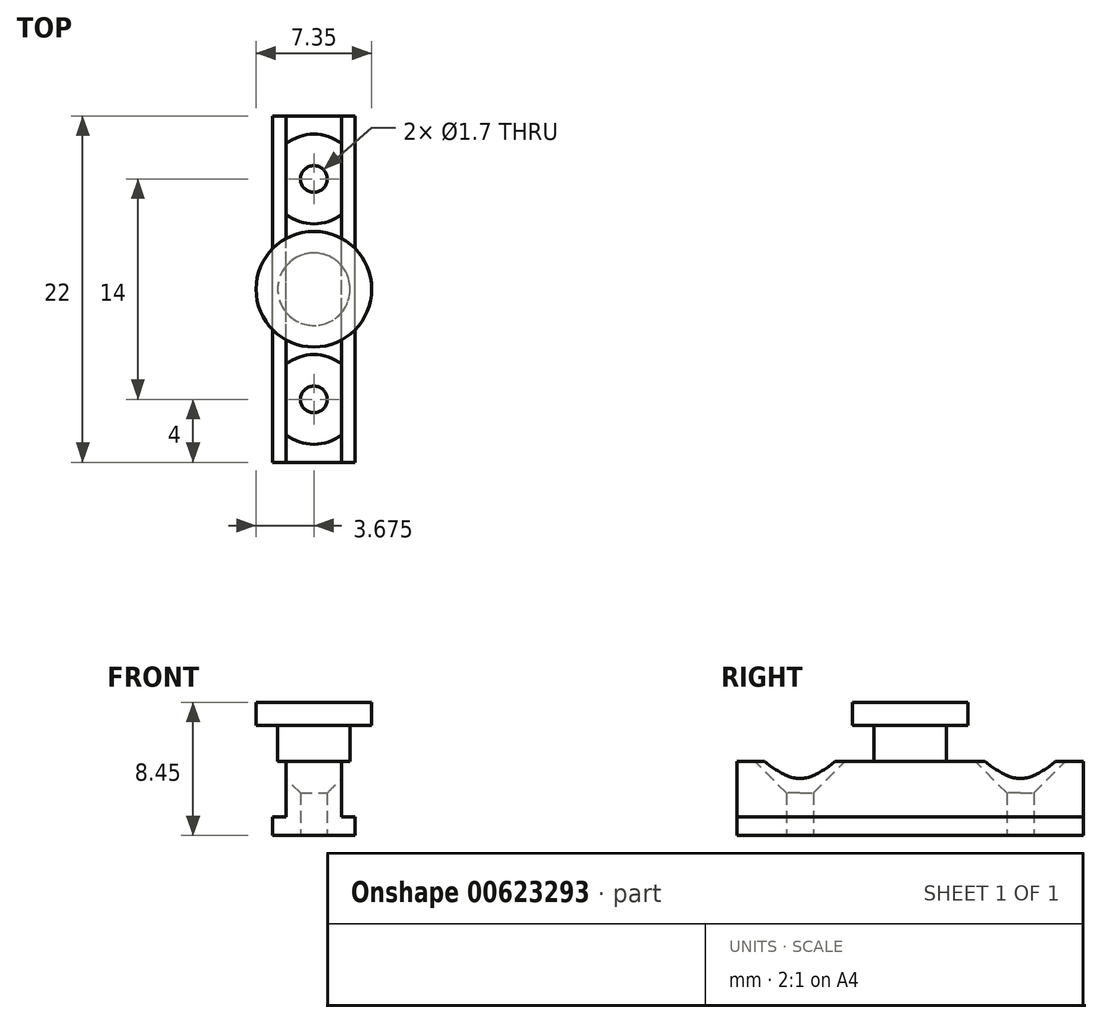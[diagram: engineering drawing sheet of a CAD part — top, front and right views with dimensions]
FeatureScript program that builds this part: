
annotation { "Feature Type Name" : "Feature", "Feature Type Description" : "" }
export const myFeature = defineFeature(function(context is Context, id is Id, definition is map)
    precondition{}
    {
        {
            var Q0;
            Q0=qCreatedBy(makeId("Front.planeOp"),FACE);
            var sketch = newSketch(context, id + "F0", { "sketchPlane" : qUnion([Q0])});
            skLineSegment(sketch, "E0.bottom", {"start": v(-39.65, 22.37) * mm, "end": v(-36.12, 22.37) * mm});
            skLineSegment(sketch, "E0.top", {"start": v(-39.65, 17.67) * mm, "end": v(-36.12, 17.67) * mm});
            skLineSegment(sketch, "E0.left", {"start": v(-39.65, 22.37) * mm, "end": v(-39.65, 18.84) * mm});
            skLineSegment(sketch, "E0.right", {"start": v(-36.12, 22.37) * mm, "end": v(-36.12, 18.84) * mm});
            skLineSegment(sketch, "E1.bottom", {"start": v(-36.12, 17.67) * mm, "end": v(-35.26, 17.67) * mm});
            skLineSegment(sketch, "E1.top", {"start": v(-36.12, 18.84) * mm, "end": v(-35.26, 18.84) * mm});
            skLineSegment(sketch, "E1.right", {"start": v(-35.26, 17.67) * mm, "end": v(-35.26, 18.84) * mm});
            skLineSegment(sketch, "E2.bottom", {"start": v(-39.65, 17.67) * mm, "end": v(-40.5, 17.67) * mm});
            skLineSegment(sketch, "E2.top", {"start": v(-39.65, 18.84) * mm, "end": v(-40.5, 18.84) * mm});
            skLineSegment(sketch, "E2.right", {"start": v(-40.5, 17.67) * mm, "end": v(-40.5, 18.84) * mm});
            skSolve(sketch);
        }
        {
            var Q0;
            Q0 = qSketchRegion(id + "F0", true);
            extrude(context, id + "F1", {"entities" : qUnion([Q0]), "depth" : 22 * mm, "offsetDistance" : 25 * mm});
        }
        {
            var Q0;
            Q0=makeQuery(id+"F1.opExtrude","SWEPT_FACE",FACE,{"disambiguationData":[OSD([sQuery(id+"F0.wireOp",EDGE,"E0.bottom")])]});
            var sketch = newSketch(context, id + "F2", { "sketchPlane" : qUnion([Q0])});
            skLineSegment(sketch, "E3", {"start": v(-39.65, 0) * mm, "end": v(-36.12, -22) * mm, "construction": true});
            skLineSegment(sketch, "E4", {"start": v(-39.65, -22) * mm, "end": v(-36.12, 0) * mm, "construction": true});
            skCircle(sketch, "E5", {"center": v(-37.88, -11) * mm, "radius": 2.3 * mm});
            skSolve(sketch);
        }
        {
            var Q0;
            {var subQ0=sQuery(id+"F2.wireOp",EDGE,"E5");var subQ1=makeQuery(id+"F1.opExtrude","SWEPT_EDGE",EDGE,{"disambiguationData":[OSD([sQuery(id+"F0.wireOp",EDGE,"E0.bottom"),sQuery(id+"F0.wireOp",EDGE,"E0.left")])]});var subQ2=makeQuery(id+"F2.imprint","INTERSECT",VERTEX,{"disambiguationData":[OD(0.0)],"derivedFrom":[subQ1,subQ0]});Q0=makeQuery(id+"F2.imprint","IMPRINT",FACE,{"disambiguationData":[TD([[makeQuery(id+"F2.imprint","IMPRINT",EDGE,{"disambiguationData":[TD([[subQ2,-1.0]])],"derivedFrom":subQ0}),1.0]])]});}
            var Q1;
            {var subQ0=sQuery(id+"F2.wireOp",EDGE,"E5");var subQ1=sQuery(id+"F0.wireOp",EDGE,"E0.bottom");var subQ2=makeQuery(id+"F1.opExtrude","SWEPT_EDGE",EDGE,{"disambiguationData":[OSD([subQ1,sQuery(id+"F0.wireOp",EDGE,"E0.left")])]});var subQ3=makeQuery(id+"F2.imprint","INTERSECT",VERTEX,{"disambiguationData":[OD(0.0)],"derivedFrom":[subQ2,subQ0]});Q1=makeQuery(id+"F2.imprint","IMPRINT",FACE,{"disambiguationData":[TD([[makeQuery(id+"F2.imprint","IMPRINT",EDGE,{"disambiguationData":[TD([[subQ3,1.0]])],"derivedFrom":subQ0}),1.0]])]});}
            var Q2;
            {var subQ0=sQuery(id+"F2.wireOp",EDGE,"E5");var subQ1=makeQuery(id+"F1.opExtrude","SWEPT_EDGE",EDGE,{"disambiguationData":[OSD([sQuery(id+"F0.wireOp",EDGE,"E0.bottom"),sQuery(id+"F0.wireOp",EDGE,"E0.right")])]});var subQ2=makeQuery(id+"F2.imprint","INTERSECT",VERTEX,{"disambiguationData":[OD(0.0)],"derivedFrom":[subQ1,subQ0]});Q2=makeQuery(id+"F2.imprint","IMPRINT",FACE,{"disambiguationData":[TD([[makeQuery(id+"F2.imprint","IMPRINT",EDGE,{"disambiguationData":[TD([[subQ2,1.0]])],"derivedFrom":subQ0}),1.0]])]});}
            extrude(context, id + "F3", {"entities" : qUnion([Q0, Q1, Q2]), "operationType" : NewBodyOperationType.ADD, "depth" : 2.3 * mm, "offsetDistance" : 25 * mm});
        }
        {
            var Q0;
            Q0=makeQuery(id+"F3.opExtrude","CAP_FACE",FACE,{"disambiguationData":[OSD([sQuery(id+"F2.wireOp",EDGE,"E5")])],"isStart":false});
            var sketch = newSketch(context, id + "F4", { "sketchPlane" : qUnion([Q0])});
            skCircle(sketch, "E6", {"center": v(-37.88, -11) * mm, "radius": 3.67 * mm});
            skSolve(sketch);
        }
        {
            var Q0;
            Q0=makeQuery(id+"F4.imprint","IMPRINT",FACE,{"disambiguationData":[TD([[makeQuery(id+"F4.imprint","IMPRINT",EDGE,{"derivedFrom":makeQuery(id+"F3.opExtrude","CAP_EDGE",EDGE,{"disambiguationData":[OSD([sQuery(id+"F2.wireOp",EDGE,"E5")])],"isStart":false})}),1.0]])]});
            var Q1;
            Q1=makeQuery(id+"F4.imprint","IMPRINT",FACE,{"disambiguationData":[TD([[makeQuery(id+"F4.imprint","IMPRINT",EDGE,{"derivedFrom":sQuery(id+"F4.wireOp",EDGE,"E6")}),1.0]])]});
            extrude(context, id + "F5", {"entities" : qUnion([Q0, Q1]), "operationType" : NewBodyOperationType.ADD, "depth" : 1.45 * mm, "offsetDistance" : 25 * mm});
        }
        {
            var Q0;
            Q0=makeQuery(id+"F1.opExtrude","SWEPT_FACE",FACE,{"disambiguationData":[OSD([sQuery(id+"F0.wireOp",EDGE,"E0.top"),sQuery(id+"F0.wireOp",EDGE,"E1.bottom"),sQuery(id+"F0.wireOp",EDGE,"E2.bottom")])]});
            var sketch = newSketch(context, id + "F6", { "sketchPlane" : qUnion([Q0])});
            skLineSegment(sketch, "E7", {"start": v(-37.88, 22) * mm, "end": v(-37.88, 0) * mm, "construction": true});
            skCircle(sketch, "E8", {"center": v(-37.88, 18) * mm, "radius": 0.85 * mm});
            skCircle(sketch, "E9", {"center": v(-37.88, 4) * mm, "radius": 0.85 * mm});
            skSolve(sketch);
        }
        {
            var Q0;
            Q0=makeQuery(id+"F6.imprint","IMPRINT",FACE,{"disambiguationData":[TD([[makeQuery(id+"F6.imprint","IMPRINT",EDGE,{"derivedFrom":sQuery(id+"F6.wireOp",EDGE,"E8")}),1.0]])]});
            var Q1;
            Q1=makeQuery(id+"F6.imprint","IMPRINT",FACE,{"disambiguationData":[TD([[makeQuery(id+"F6.imprint","IMPRINT",EDGE,{"derivedFrom":sQuery(id+"F6.wireOp",EDGE,"E9")}),1.0]])]});
            extrude(context, id + "F7", {"entities" : qUnion([Q0, Q1]), "operationType" : NewBodyOperationType.REMOVE, "oppositeDirection" : true, "depth" : 25 * mm, "offsetDistance" : 25 * mm});
        }
        {
            var Q0;
            {var subQ1=sQuery(id+"F0.wireOp",EDGE,"E0.right");var subQ2=sQuery(id+"F0.wireOp",EDGE,"E0.left");var subQ3=sQuery(id+"F0.wireOp",EDGE,"E0.bottom");Q0=makeQuery(id+"F7.boolean.opBoolean","INTERSECT",EDGE,{"derivedFrom":[makeQuery(id+"F3.boolean.opBoolean","SPLIT",FACE,{"disambiguationData":[TD([makeQuery(id+"F1.opExtrude","CAP_FACE",FACE,{"disambiguationData":[OSD([subQ3,sQuery(id+"F0.wireOp",EDGE,"E0.top"),subQ2,subQ1,sQuery(id+"F0.wireOp",EDGE,"E1.bottom"),sQuery(id+"F0.wireOp",EDGE,"E1.top"),sQuery(id+"F0.wireOp",EDGE,"E1.right"),sQuery(id+"F0.wireOp",EDGE,"E2.bottom"),sQuery(id+"F0.wireOp",EDGE,"E2.top"),sQuery(id+"F0.wireOp",EDGE,"E2.right")])],"isStart":false})])],"derivedFrom":makeQuery(id+"F1.opExtrude","SWEPT_FACE",FACE,{"disambiguationData":[OSD([subQ3])]})}),makeQuery(id+"F7.opExtrude","SWEPT_FACE",FACE,{"disambiguationData":[OSD([sQuery(id+"F6.wireOp",EDGE,"E8")])]})]});}
            chamfer(context, id + "F8", {"entities" : qUnion([Q0]), "width" : 2 * mm, "tangentPropagation" : true});
        }
        {
            var Q0;
            {var subQ1=sQuery(id+"F0.wireOp",EDGE,"E0.right");var subQ2=sQuery(id+"F0.wireOp",EDGE,"E0.left");var subQ3=sQuery(id+"F0.wireOp",EDGE,"E0.bottom");Q0=makeQuery(id+"F7.boolean.opBoolean","INTERSECT",EDGE,{"derivedFrom":[makeQuery(id+"F3.boolean.opBoolean","SPLIT",FACE,{"disambiguationData":[TD([makeQuery(id+"F1.opExtrude","CAP_FACE",FACE,{"disambiguationData":[OSD([subQ3,sQuery(id+"F0.wireOp",EDGE,"E0.top"),subQ2,subQ1,sQuery(id+"F0.wireOp",EDGE,"E1.bottom"),sQuery(id+"F0.wireOp",EDGE,"E1.top"),sQuery(id+"F0.wireOp",EDGE,"E1.right"),sQuery(id+"F0.wireOp",EDGE,"E2.bottom"),sQuery(id+"F0.wireOp",EDGE,"E2.top"),sQuery(id+"F0.wireOp",EDGE,"E2.right")])],"isStart":true})])],"derivedFrom":makeQuery(id+"F1.opExtrude","SWEPT_FACE",FACE,{"disambiguationData":[OSD([subQ3])]})}),makeQuery(id+"F7.opExtrude","SWEPT_FACE",FACE,{"disambiguationData":[OSD([sQuery(id+"F6.wireOp",EDGE,"E9")])]})]});}
            chamfer(context, id + "F9", {"entities" : qUnion([Q0]), "width" : 2 * mm, "tangentPropagation" : true});
        }
    });
